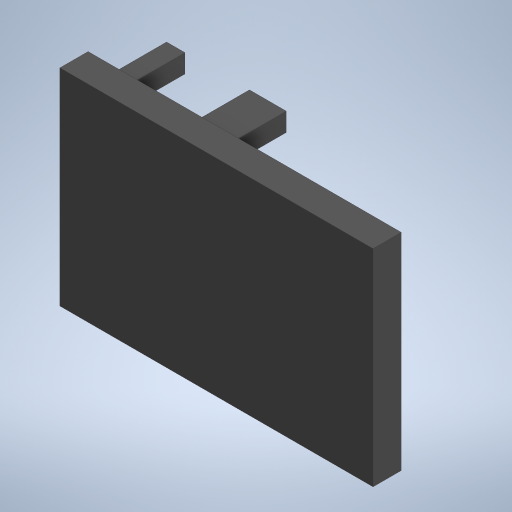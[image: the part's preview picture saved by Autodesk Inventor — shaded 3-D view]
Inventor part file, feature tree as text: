
AUTODESK INVENTOR PART (.ipt)
format: ipt  version: 2023.1 (Build 271208000, 208)  size: 419,840 bytes
history: native  units: mm
features: extrude x6, sketch x5, projected_geometry x2, fillet x1
ambient origin geometry x8: Origin, YZ Plane, XZ Plane, XY Plane, X Axis, Y Axis, Z Axis, Center Point
bodies: Body1 (feature_tree)
feature tree (14):
  extrude  "돌출2"  Depth=85.0mm
  extrude  "돌출3"  Depth=56.0mm
  sketch  "스케치5"
  extrude  "돌출4"  Depth=7.65mm TaperAngle=0.0deg
  fillet  "모깎기1"  Radius=5.0mm
  extrude  "돌출5"  Depth=5.0mm
  extrude  "돌출6"  Depth=0.6mm
  extrude  "돌출7"  Depth=0.6mm
  sketch  "스케치2"
  sketch  "스케치4"
  sketch  "스케치6"
  projected_geometry  "투영된 루프1"
  sketch  "스케치7"
  projected_geometry  "투영된 루프2"
